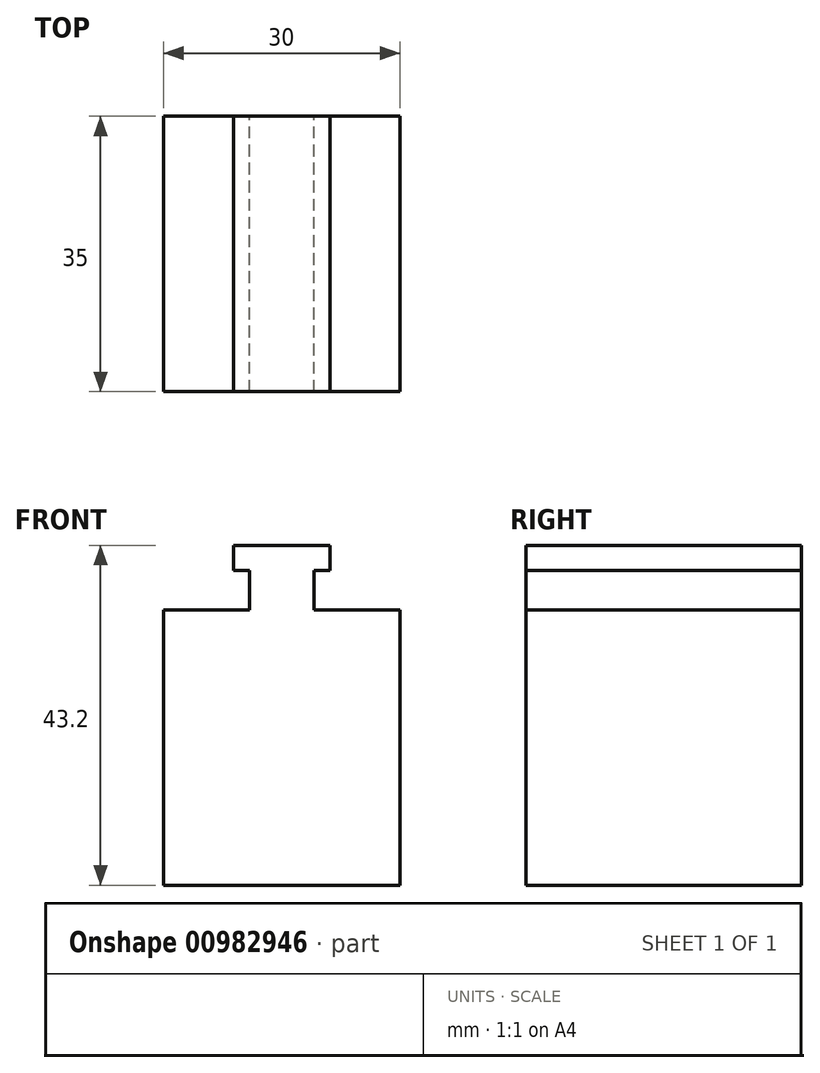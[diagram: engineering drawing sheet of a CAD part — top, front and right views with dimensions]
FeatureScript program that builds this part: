
annotation { "Feature Type Name" : "Feature", "Feature Type Description" : "" }
export const myFeature = defineFeature(function(context is Context, id is Id, definition is map)
    precondition{}
    {
        {
            var Q0;
            Q0=qCreatedBy(makeId("Front.planeOp"),FACE);
            var sketch = newSketch(context, id + "F0", { "sketchPlane" : qUnion([Q0])});
            skLineSegment(sketch, "E0", {"start": v(-6.12, 0) * mm, "end": v(-4.1, 0) * mm});
            skLineSegment(sketch, "E1", {"start": v(-4.1, 0) * mm, "end": v(-4.1, -5) * mm});
            skLineSegment(sketch, "E2", {"start": v(-4.1, -5) * mm, "end": v(-11.1, -5) * mm});
            skLineSegment(sketch, "E3", {"start": v(-11.1, -5) * mm, "end": v(-21.1, 15) * mm});
            skLineSegment(sketch, "E4", {"start": v(-6.12, 0) * mm, "end": v(-6.12, 3.2) * mm});
            skLineSegment(sketch, "E5", {"start": v(-6.12, 3.2) * mm, "end": v(0, 3.2) * mm});
            skLineSegment(sketch, "E6", {"start": v(-21.1, 15) * mm, "end": v(-48, 15) * mm});
            skLineSegment(sketch, "E7", {"start": v(-48, 15) * mm, "end": v(-48, 50) * mm});
            skLineSegment(sketch, "E8", {"start": v(-48, 50) * mm, "end": v(-42, 50) * mm});
            skLineSegment(sketch, "E9", {"start": v(-42, 50) * mm, "end": v(-42, 30) * mm});
            skLineSegment(sketch, "E10", {"start": v(-42, 30) * mm, "end": v(0, 30) * mm});
            skLineSegment(sketch, "E11", {"start": v(-42, 50) * mm, "end": v(0, 50) * mm});
            skLineSegment(sketch, "E12", {"start": v(0, 3.2) * mm, "end": v(0, 50) * mm, "construction": true});
            skLineSegment(sketch, "E13.MirrorCS", {"start": v(6.12, 0) * mm, "end": v(4.1, 0) * mm});
            skLineSegment(sketch, "E14.MirrorCS", {"start": v(6.12, 3.2) * mm, "end": v(0, 3.2) * mm});
            skLineSegment(sketch, "E15.MirrorCS", {"start": v(42, 50) * mm, "end": v(0, 50) * mm});
            skLineSegment(sketch, "E16.MirrorCS", {"start": v(6.12, 0) * mm, "end": v(6.12, 3.2) * mm});
            skLineSegment(sketch, "E17.MirrorCS", {"start": v(42, 30) * mm, "end": v(0, 30) * mm});
            skLineSegment(sketch, "E18.MirrorCS", {"start": v(11.1, -5) * mm, "end": v(21.1, 15) * mm});
            skLineSegment(sketch, "E19.MirrorCS", {"start": v(42, 50) * mm, "end": v(42, 30) * mm});
            skLineSegment(sketch, "E20.MirrorCS", {"start": v(4.1, -5) * mm, "end": v(11.1, -5) * mm});
            skLineSegment(sketch, "E21.MirrorCS", {"start": v(48, 50) * mm, "end": v(42, 50) * mm});
            skLineSegment(sketch, "E22.MirrorCS", {"start": v(4.1, 0) * mm, "end": v(4.1, -5) * mm});
            skLineSegment(sketch, "E23.MirrorCS", {"start": v(48, 15) * mm, "end": v(48, 50) * mm});
            skLineSegment(sketch, "E24.MirrorCS", {"start": v(21.1, 15) * mm, "end": v(48, 15) * mm});
            skLineSegment(sketch, "E25.bottom", {"start": v(15, -5) * mm, "end": v(-15, -5) * mm});
            skLineSegment(sketch, "E25.top", {"start": v(15, -40) * mm, "end": v(-15, -40) * mm});
            skLineSegment(sketch, "E25.left", {"start": v(15, -5) * mm, "end": v(15, -40) * mm});
            skLineSegment(sketch, "E25.right", {"start": v(-15, -5) * mm, "end": v(-15, -40) * mm});
            skPoint(sketch, "E25.middle", {"position": v(0, -22.5) * mm});
            skSolve(sketch);
        }
        {
            var Q0;
            Q0=makeQuery(id+"F0.imprint","IMPRINT",FACE,{"disambiguationData":[TD([[makeQuery(id+"F0.imprint","IMPRINT",EDGE,{"derivedFrom":sQuery(id+"F0.wireOp",EDGE,"E0")}),1.0]])]});
            var Q1;
            {var subQ1=sQuery(id+"F0.wireOp",EDGE,"E2");Q1=makeQuery(id+"F0.imprint","IMPRINT",FACE,{"disambiguationData":[TD([[makeQuery(id+"F0.imprint","IMPRINT",EDGE,{"derivedFrom":subQ1}),1.0]])]});}
            extrude(context, id + "F1", {"entities" : qUnion([Q0, Q1]), "depth" : 35 * mm, "offsetDistance" : 25 * mm});
        }
    });
